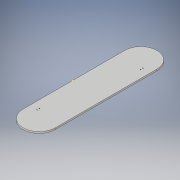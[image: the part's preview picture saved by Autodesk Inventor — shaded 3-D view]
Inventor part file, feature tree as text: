
AUTODESK INVENTOR PART (.ipt)
format: ipt  version: 2019 (Build 230136000, 136)  size: 133,120 bytes
history: native  units: mm
features: sketch x4, hole x2, other x1, extrude x1
ambient origin geometry x8: Origin, YZ Plane, XZ Plane, XY Plane, X Axis, Y Axis, Z Axis, Center Point
bodies: Body1 (feature_tree)
feature tree (8):
  other  "ソリッド1"
  sketch  "スケッチ1"
  extrude  "押し出し1"  Depth=270.0mm
  hole  "穴4"  [1 undecoded]
  hole  "穴5"  [1 undecoded]
  sketch  "スケッチ2"
  sketch  "スケッチ6"
  sketch  "スケッチ7"
note: 2 required parameter values undecoded (feature->parameter linkage not recoverable at this tier; creation-order binding heuristic only, values carry confidence <= 0.55)
